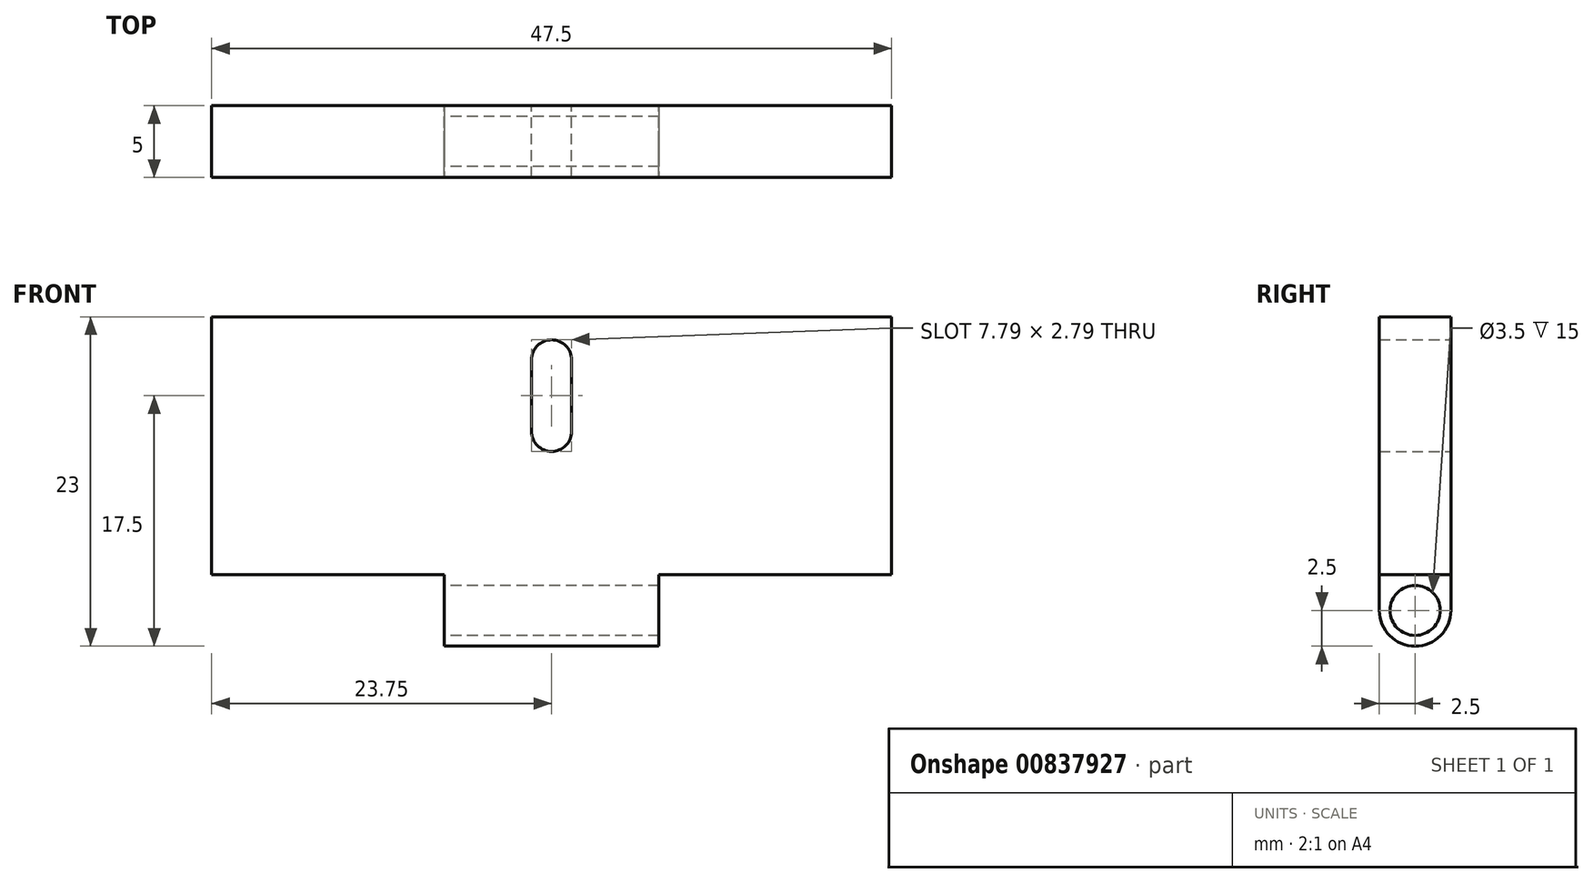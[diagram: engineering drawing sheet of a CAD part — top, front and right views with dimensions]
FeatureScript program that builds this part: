
annotation { "Feature Type Name" : "Feature", "Feature Type Description" : "" }
export const myFeature = defineFeature(function(context is Context, id is Id, definition is map)
    precondition{}
    {
        {
            var Q0;
            Q0=qCreatedBy(makeId("Front.planeOp"),FACE);
            var sketch = newSketch(context, id + "F0", { "sketchPlane" : qUnion([Q0])});
            skLineSegment(sketch, "E0.bottom", {"start": v(23.75, -9) * mm, "end": v(-23.75, -9) * mm});
            skLineSegment(sketch, "E0.top", {"start": v(23.75, 9) * mm, "end": v(-23.75, 9) * mm});
            skLineSegment(sketch, "E0.left", {"start": v(23.75, -9) * mm, "end": v(23.75, 9) * mm});
            skLineSegment(sketch, "E0.right", {"start": v(-23.75, -9) * mm, "end": v(-23.75, 9) * mm});
            skPoint(sketch, "E0.middle", {"position": v(0, 0) * mm});
            skArc(sketch, "E1", {"start": v(-1.4, 1) * mm, "mid": v(0, -0.4) * mm, "end": v(1.4, 1) * mm});
            skArc(sketch, "E2", {"start": v(1.4, 6) * mm, "mid": v(0, 7.4) * mm, "end": v(-1.4, 6) * mm});
            skLineSegment(sketch, "E3", {"start": v(1.4, 1) * mm, "end": v(1.4, 6) * mm});
            skLineSegment(sketch, "E4", {"start": v(-1.4, 1) * mm, "end": v(-1.4, 6) * mm});
            skSolve(sketch);
        }
        {
            var Q0;
            Q0=makeQuery(id+"F0.imprint","IMPRINT",FACE,{"disambiguationData":[TD([[makeQuery(id+"F0.imprint","IMPRINT",EDGE,{"derivedFrom":sQuery(id+"F0.wireOp",EDGE,"E0.bottom")}),-1.0]])]});
            extrude(context, id + "F1", {"entities" : qUnion([Q0]), "depth" : 5 * mm, "offsetDistance" : 25 * mm});
        }
        {
            var Q0;
            Q0=makeQuery(id+"F1.opExtrude","SWEPT_FACE",FACE,{"disambiguationData":[OSD([sQuery(id+"F0.wireOp",EDGE,"E0.bottom")])]});
            var sketch = newSketch(context, id + "F2", { "sketchPlane" : qUnion([Q0])});
            skLineSegment(sketch, "E5", {"start": v(0, 5) * mm, "end": v(0, 0) * mm});
            skPoint(sketch, "E6.start.orphan", {"position": v(0, 2.5) * mm});
            skSolve(sketch);
        }
        {
            var Q0;
            Q0=qCreatedBy(makeId("Right.planeOp"),FACE);
            var sketch = newSketch(context, id + "F3", { "sketchPlane" : qUnion([Q0])});
            skCircle(sketch, "E7", {"center": v(-2.5, -11.5) * mm, "radius": 2.5 * mm});
            skPoint(sketch, "E8", {"position": v(0, -11.5) * mm});
            skPoint(sketch, "E9", {"position": v(-5, -11.5) * mm});
            skCircle(sketch, "E10", {"center": v(-2.5, -11.5) * mm, "radius": 1.75 * mm});
            skLineSegment(sketch, "E11", {"start": v(0, -11.5) * mm, "end": v(0, -9) * mm});
            skLineSegment(sketch, "E12", {"start": v(0, -9) * mm, "end": v(-5, -9) * mm});
            skLineSegment(sketch, "E13", {"start": v(-5, -9) * mm, "end": v(-5, -11.5) * mm});
            skSolve(sketch);
        }
        {
            var Q0;
            Q0=makeQuery(id+"F3.imprint","IMPRINT",FACE,{"disambiguationData":[TD([[makeQuery(id+"F3.imprint","IMPRINT",EDGE,{"derivedFrom":sQuery(id+"F3.wireOp",EDGE,"E10")}),-1.0]])]});
            var Q1;
            {var subQ0=sQuery(id+"F3.wireOp",EDGE,"E11");Q1=makeQuery(id+"F3.imprint","IMPRINT",FACE,{"disambiguationData":[TD([[makeQuery(id+"F3.imprint","IMPRINT",EDGE,{"derivedFrom":subQ0}),1.0]])]});}
            var Q2;
            {var subQ0=sQuery(id+"F3.wireOp",EDGE,"E13");Q2=makeQuery(id+"F3.imprint","IMPRINT",FACE,{"disambiguationData":[TD([[makeQuery(id+"F3.imprint","IMPRINT",EDGE,{"derivedFrom":subQ0}),1.0]])]});}
            extrude(context, id + "F4", {"entities" : qUnion([Q0, Q1, Q2]), "operationType" : NewBodyOperationType.ADD, "endBound" : BoundingType.SYMMETRIC, "depth" : 15 * mm, "offsetDistance" : 25 * mm});
        }
    });
